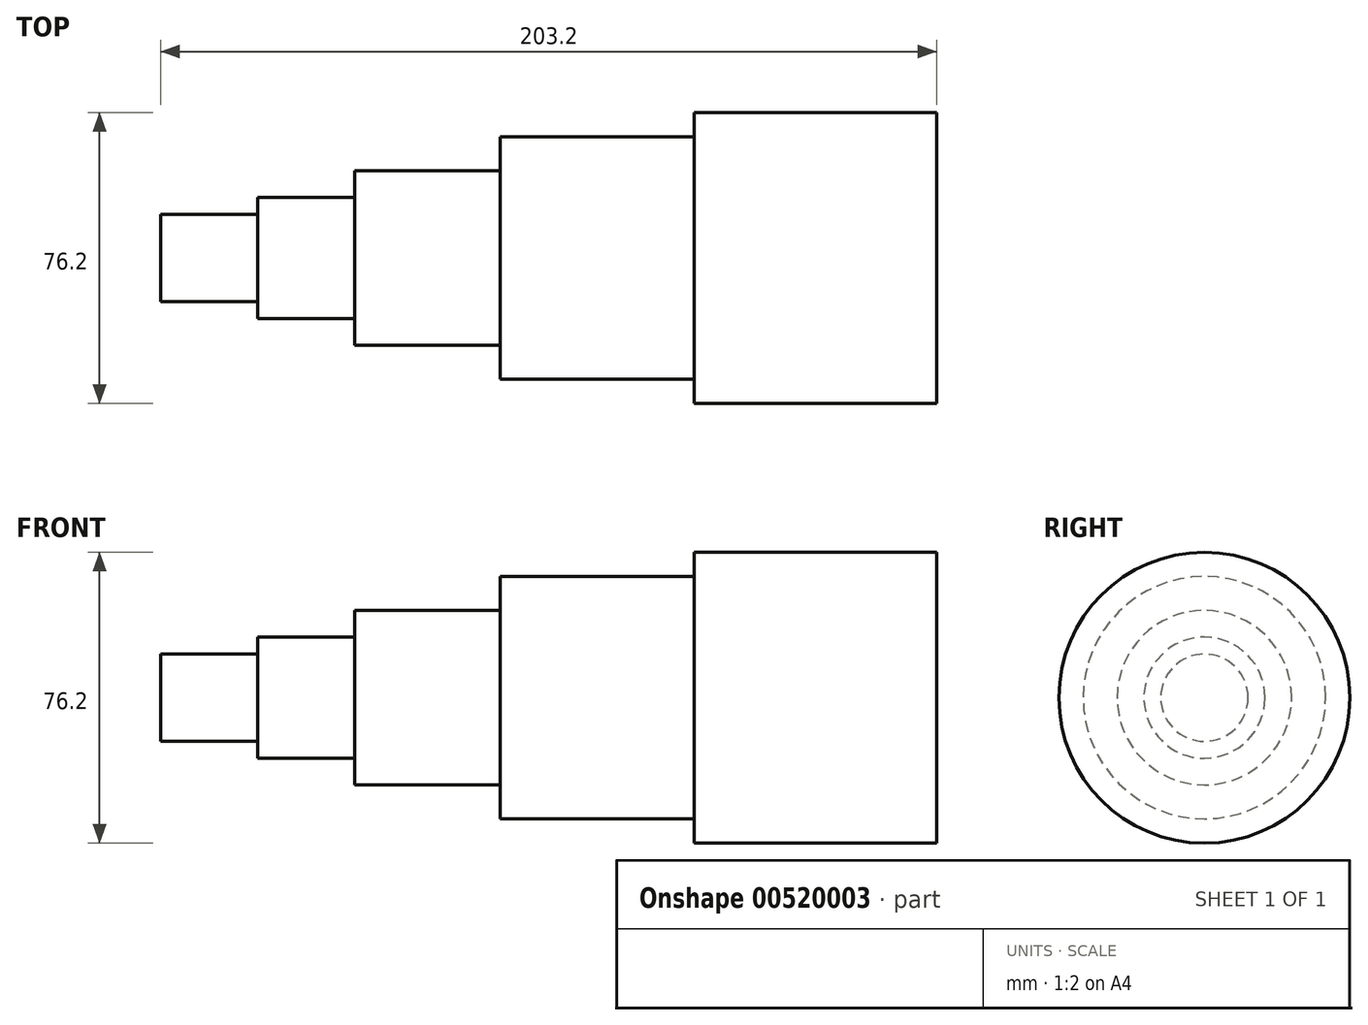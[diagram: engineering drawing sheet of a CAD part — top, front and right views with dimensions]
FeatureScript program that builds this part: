
annotation { "Feature Type Name" : "Feature", "Feature Type Description" : "" }
export const myFeature = defineFeature(function(context is Context, id is Id, definition is map)
    precondition{}
    {
        {
            var Q0;
            Q0=qCreatedBy(makeId("Right.planeOp"),FACE);
            var sketch = newSketch(context, id + "F0", { "sketchPlane" : qUnion([Q0])});
            skCircle(sketch, "E0", {"center": v(0, 0) * mm, "radius": 38.1 * mm});
            skSolve(sketch);
        }
        {
            var Q0;
            Q0=makeQuery(id+"F0.imprint","IMPRINT",FACE,{"disambiguationData":[TD([[makeQuery(id+"F0.imprint","IMPRINT",EDGE,{"derivedFrom":sQuery(id+"F0.wireOp",EDGE,"E0")}),1.0]])]});
            extrude(context, id + "F1", {"entities" : qUnion([Q0]), "depth" : 203.2 * mm, "offsetDistance" : 25.4 * mm});
        }
        {
            var Q0;
            Q0=makeQuery(id+"F1.opExtrude","CAP_FACE",FACE,{"disambiguationData":[OSD([sQuery(id+"F0.wireOp",EDGE,"E0")])],"isStart":true});
            var sketch = newSketch(context, id + "F2", { "sketchPlane" : qUnion([Q0])});
            skCircle(sketch, "E1", {"center": v(0, 0) * mm, "radius": 31.75 * mm});
            skSolve(sketch);
        }
        {
            var Q0;
            Q0=makeQuery(id+"F2.imprint","IMPRINT",FACE,{"disambiguationData":[TD([[makeQuery(id+"F2.imprint","IMPRINT",EDGE,{"derivedFrom":sQuery(id+"F2.wireOp",EDGE,"E1")}),-1.0]])]});
            extrude(context, id + "F3", {"entities" : qUnion([Q0]), "operationType" : NewBodyOperationType.REMOVE, "oppositeDirection" : true, "depth" : 139.7 * mm, "offsetDistance" : 25.4 * mm});
        }
        {
            var Q0;
            Q0=makeQuery(id+"F2.imprint","IMPRINT",FACE,{"disambiguationData":[TD([[makeQuery(id+"F2.imprint","IMPRINT",EDGE,{"derivedFrom":sQuery(id+"F2.wireOp",EDGE,"E1")}),1.0]])]});
            var sketch = newSketch(context, id + "F4", { "sketchPlane" : qUnion([Q0])});
            skCircle(sketch, "E2", {"center": v(0, 0) * mm, "radius": 22.86 * mm});
            skSolve(sketch);
        }
        {
            var Q0;
            Q0=makeQuery(id+"F4.imprint","IMPRINT",FACE,{"disambiguationData":[TD([[makeQuery(id+"F4.imprint","IMPRINT",EDGE,{"derivedFrom":sQuery(id+"F4.wireOp",EDGE,"E2")}),-1.0]])]});
            extrude(context, id + "F5", {"entities" : qUnion([Q0]), "operationType" : NewBodyOperationType.REMOVE, "oppositeDirection" : true, "depth" : 88.9 * mm, "offsetDistance" : 25.4 * mm});
        }
        {
            var Q0;
            Q0=makeQuery(id+"F2.imprint","IMPRINT",FACE,{"disambiguationData":[TD([[makeQuery(id+"F2.imprint","IMPRINT",EDGE,{"derivedFrom":sQuery(id+"F2.wireOp",EDGE,"E1")}),1.0]])]});
            var sketch = newSketch(context, id + "F6", { "sketchPlane" : qUnion([Q0])});
            skCircle(sketch, "E3", {"center": v(0, 0) * mm, "radius": 15.88 * mm});
            skSolve(sketch);
        }
        {
            var Q0;
            Q0=makeQuery(id+"F6.imprint","IMPRINT",FACE,{"disambiguationData":[TD([[makeQuery(id+"F6.imprint","IMPRINT",EDGE,{"derivedFrom":sQuery(id+"F6.wireOp",EDGE,"E3")}),-1.0]])]});
            extrude(context, id + "F7", {"entities" : qUnion([Q0]), "operationType" : NewBodyOperationType.REMOVE, "oppositeDirection" : true, "depth" : 50.8 * mm, "offsetDistance" : 25.4 * mm});
        }
        {
            var Q0;
            Q0=makeQuery(id+"F1.opExtrude","CAP_FACE",FACE,{"disambiguationData":[OSD([sQuery(id+"F0.wireOp",EDGE,"E0")])],"isStart":true});
            var sketch = newSketch(context, id + "F8", { "sketchPlane" : qUnion([Q0])});
            skCircle(sketch, "E4", {"center": v(0, 0) * mm, "radius": 11.43 * mm});
            skSolve(sketch);
        }
        {
            var Q0;
            Q0=makeQuery(id+"F8.imprint","IMPRINT",FACE,{"disambiguationData":[TD([[makeQuery(id+"F8.imprint","IMPRINT",EDGE,{"derivedFrom":sQuery(id+"F8.wireOp",EDGE,"E4")}),-1.0]])]});
            extrude(context, id + "F9", {"entities" : qUnion([Q0]), "operationType" : NewBodyOperationType.REMOVE, "oppositeDirection" : true, "depth" : 25.4 * mm, "offsetDistance" : 25.4 * mm});
        }
    });
